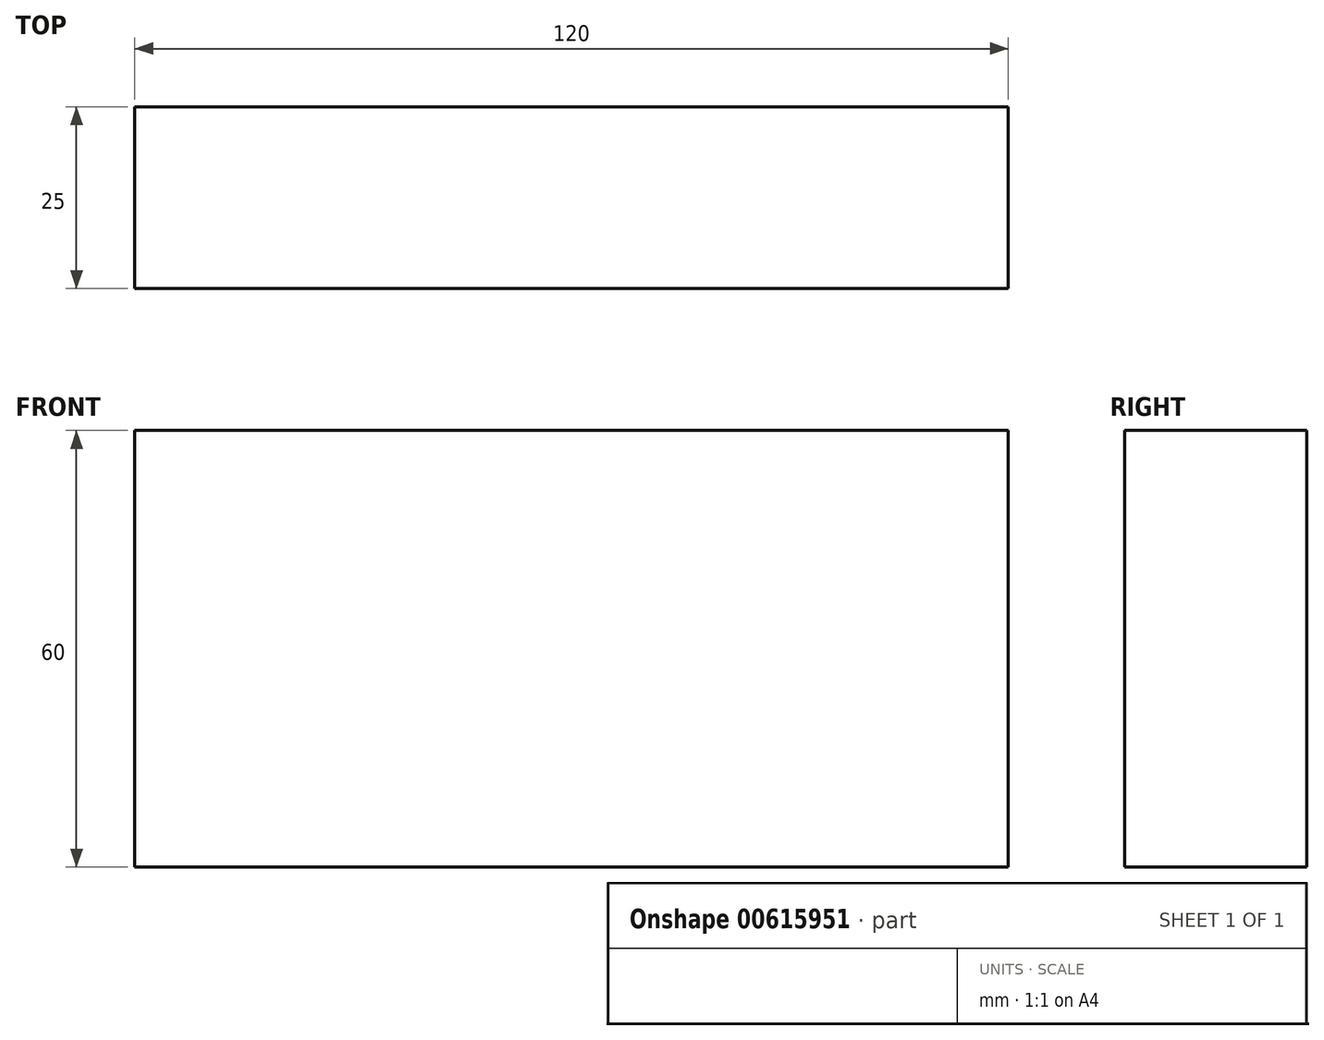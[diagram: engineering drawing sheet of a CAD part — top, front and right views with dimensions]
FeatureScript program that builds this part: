
annotation { "Feature Type Name" : "Feature", "Feature Type Description" : "" }
export const myFeature = defineFeature(function(context is Context, id is Id, definition is map)
    precondition{}
    {
        {
            var Q0;
            Q0=qCreatedBy(makeId("Front.planeOp"),FACE);
            var sketch = newSketch(context, id + "F0", { "sketchPlane" : qUnion([Q0])});
            skLineSegment(sketch, "E0.bottom", {"start": v(-53.6, 60) * mm, "end": v(66.4, 60) * mm});
            skLineSegment(sketch, "E0.top", {"start": v(-53.6, 0) * mm, "end": v(66.4, 0) * mm});
            skLineSegment(sketch, "E0.left", {"start": v(-53.6, 60) * mm, "end": v(-53.6, 0) * mm});
            skLineSegment(sketch, "E0.right", {"start": v(66.4, 60) * mm, "end": v(66.4, 0) * mm});
            skSolve(sketch);
        }
        {
            var Q0;
            Q0=makeQuery(id+"F0.imprint","IMPRINT",FACE,{"disambiguationData":[TD([[makeQuery(id+"F0.imprint","IMPRINT",EDGE,{"derivedFrom":sQuery(id+"F0.wireOp",EDGE,"E0.bottom")}),-1.0]])]});
            extrude(context, id + "F1", {"entities" : qUnion([Q0]), "depth" : 25 * mm, "offsetDistance" : 25 * mm});
        }
    });
